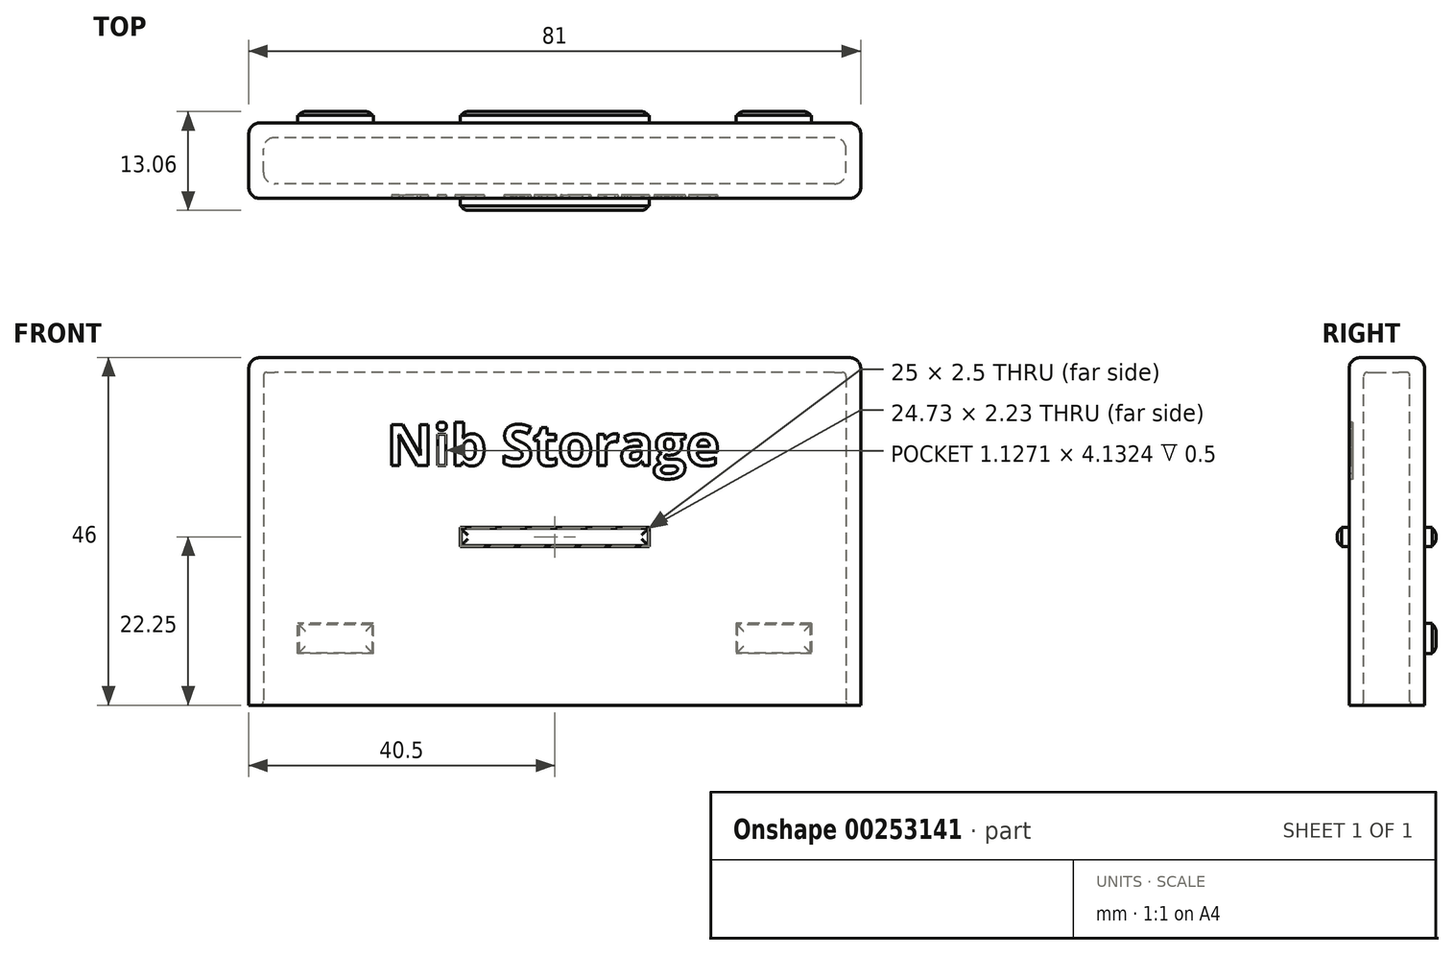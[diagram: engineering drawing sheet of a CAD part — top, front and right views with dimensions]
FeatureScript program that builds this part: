
annotation { "Feature Type Name" : "Feature", "Feature Type Description" : "" }
export const myFeature = defineFeature(function(context is Context, id is Id, definition is map)
    precondition{}
    {
        {
            var Q0;
            Q0=qCreatedBy(makeId("Top.planeOp"),FACE);
            var sketch = newSketch(context, id + "F0", { "sketchPlane" : qUnion([Q0])});
            skLineSegment(sketch, "E0.bottom", {"start": v(40.5, -5) * mm, "end": v(-40.5, -5) * mm});
            skLineSegment(sketch, "E0.top", {"start": v(40.5, 5) * mm, "end": v(-40.5, 5) * mm});
            skLineSegment(sketch, "E0.left", {"start": v(40.5, -5) * mm, "end": v(40.5, 5) * mm});
            skLineSegment(sketch, "E0.right", {"start": v(-40.5, -5) * mm, "end": v(-40.5, 5) * mm});
            skPoint(sketch, "E0.middle", {"position": v(0, 0) * mm});
            skSolve(sketch);
        }
        {
            var Q0;
            Q0=qSketchRegion(id+"F0",true);
            extrude(context, id + "F1", {"entities" : qUnion([Q0]), "depth" : 46 * mm});
        }
        {
            var Q0;
            Q0=makeQuery(id+"F1.opExtrude","CAP_EDGE",EDGE,{"disambiguationData":[OSD([sQuery(id+"F0.wireOp",EDGE,"E0.top")])],"isStart":false});
            var Q1;
            Q1=makeQuery(id+"F1.opExtrude","CAP_EDGE",EDGE,{"disambiguationData":[OSD([sQuery(id+"F0.wireOp",EDGE,"E0.bottom")])],"isStart":false});
            var Q2;
            Q2=makeQuery(id+"F1.opExtrude","CAP_EDGE",EDGE,{"disambiguationData":[OSD([sQuery(id+"F0.wireOp",EDGE,"E0.right")])],"isStart":false});
            var Q3;
            Q3=makeQuery(id+"F1.opExtrude","CAP_EDGE",EDGE,{"disambiguationData":[OSD([sQuery(id+"F0.wireOp",EDGE,"E0.left")])],"isStart":false});
            var Q4;
            Q4=makeQuery(id+"F1.opExtrude","SWEPT_EDGE",EDGE,{"disambiguationData":[OSD([sQuery(id+"F0.wireOp",EDGE,"E0.top"),sQuery(id+"F0.wireOp",EDGE,"E0.right")])]});
            var Q5;
            Q5=makeQuery(id+"F1.opExtrude","SWEPT_EDGE",EDGE,{"disambiguationData":[OSD([sQuery(id+"F0.wireOp",EDGE,"E0.bottom"),sQuery(id+"F0.wireOp",EDGE,"E0.right")])]});
            var Q6;
            Q6=makeQuery(id+"F1.opExtrude","SWEPT_EDGE",EDGE,{"disambiguationData":[OSD([sQuery(id+"F0.wireOp",EDGE,"E0.top"),sQuery(id+"F0.wireOp",EDGE,"E0.left")])]});
            var Q7;
            Q7=makeQuery(id+"F1.opExtrude","SWEPT_EDGE",EDGE,{"disambiguationData":[OSD([sQuery(id+"F0.wireOp",EDGE,"E0.bottom"),sQuery(id+"F0.wireOp",EDGE,"E0.left")])]});
            fillet(context, id + "F2", {"entities" : qUnion([Q0, Q1, Q2, Q3, Q4, Q5, Q6, Q7]), "radius" : 1.5 * mm, "tangentPropagation" : true, "allowEdgeOverflow" : false});
        }
        {
            var Q0;
            Q0=makeQuery(id+"F1.opExtrude","CAP_FACE",FACE,{"disambiguationData":[OSD([sQuery(id+"F0.wireOp",EDGE,"E0.bottom"),sQuery(id+"F0.wireOp",EDGE,"E0.top"),sQuery(id+"F0.wireOp",EDGE,"E0.left"),sQuery(id+"F0.wireOp",EDGE,"E0.right")])],"isStart":true});
            shell(context, id + "F3", {"entities" : qUnion([Q0]), "thickness" : 1.94 * mm});
        }
        {
            var Q0;
            Q0=makeQuery(id+"F3.opShell","OFFSET_EDGE",EDGE,{"disambiguationData":[OSD([sQuery(id+"F0.wireOp",EDGE,"E0.top"),sQuery(id+"F0.wireOp",EDGE,"E0.left")])]});
            var Q1;
            Q1=makeQuery(id+"F3.opShell","OFFSET_EDGE",EDGE,{"disambiguationData":[OSD([sQuery(id+"F0.wireOp",EDGE,"E0.bottom"),sQuery(id+"F0.wireOp",EDGE,"E0.left")])]});
            var Q2;
            Q2=makeQuery(id+"F3.opShell","OFFSET_EDGE",EDGE,{"disambiguationData":[OSD([sQuery(id+"F0.wireOp",EDGE,"E0.bottom"),sQuery(id+"F0.wireOp",EDGE,"E0.right")])]});
            var Q3;
            Q3=makeQuery(id+"F3.opShell","OFFSET_EDGE",EDGE,{"disambiguationData":[OSD([sQuery(id+"F0.wireOp",EDGE,"E0.top"),sQuery(id+"F0.wireOp",EDGE,"E0.right")])]});
            fillet(context, id + "F4", {"entities" : qUnion([Q0, Q1, Q2, Q3]), "radius" : 1.5 * mm, "tangentPropagation" : true, "allowEdgeOverflow" : false});
        }
        {
            var Q0;
            Q0=makeQuery(id+"F1.opExtrude","SWEPT_FACE",FACE,{"disambiguationData":[OSD([sQuery(id+"F0.wireOp",EDGE,"E0.bottom")])]});
            var sketch = newSketch(context, id + "F5", { "sketchPlane" : qUnion([Q0])});
            skLineSegment(sketch, "E1", {"start": v(39, 22.25) * mm, "end": v(-39, 22.25) * mm, "construction": true});
            skLineSegment(sketch, "E2", {"start": v(0, 44.5) * mm, "end": v(0, 0) * mm, "construction": true});
            skLineSegment(sketch, "E3.bottom", {"start": v(-12.5, 23.5) * mm, "end": v(12.5, 23.5) * mm});
            skLineSegment(sketch, "E3.top", {"start": v(-12.5, 21) * mm, "end": v(12.5, 21) * mm});
            skLineSegment(sketch, "E3.left", {"start": v(-12.5, 23.5) * mm, "end": v(-12.5, 21) * mm});
            skLineSegment(sketch, "E3.right", {"start": v(12.5, 23.5) * mm, "end": v(12.5, 21) * mm});
            skPoint(sketch, "E3.middle", {"position": v(0, 22.25) * mm});
            skLineSegment(sketch, "E4", {"start": v(-39, 8.04) * mm, "end": v(39, 8.04) * mm, "construction": true});
            skSolve(sketch);
        }
        {
            var Q0;
            Q0=qSketchRegion(id+"F5",true);
            extrude(context, id + "F6", {"entities" : qUnion([Q0]), "operationType" : NewBodyOperationType.ADD, "depth" : 1.56 * mm});
        }
        {
            var Q0;
            Q0=makeQuery(id+"F6.opExtrude","CAP_EDGE",EDGE,{"disambiguationData":[OSD([sQuery(id+"F5.wireOp",EDGE,"E3.bottom")])],"isStart":false});
            var Q1;
            Q1=makeQuery(id+"F6.opExtrude","CAP_EDGE",EDGE,{"disambiguationData":[OSD([sQuery(id+"F5.wireOp",EDGE,"E3.right")])],"isStart":false});
            var Q2;
            Q2=makeQuery(id+"F6.opExtrude","CAP_EDGE",EDGE,{"disambiguationData":[OSD([sQuery(id+"F5.wireOp",EDGE,"E3.top")])],"isStart":false});
            var Q3;
            Q3=makeQuery(id+"F6.opExtrude","CAP_EDGE",EDGE,{"disambiguationData":[OSD([sQuery(id+"F5.wireOp",EDGE,"E3.left")])],"isStart":false});
            var Q4;
            Q4=makeQuery(id+"F6.opExtrude","CAP_EDGE",EDGE,{"disambiguationData":[OSD([sQuery(id+"F5.wireOp",EDGE,"PPb5qhu8-9LVF-MKHu-zQhD-LhnvQhcufIGx.top")])],"isStart":false});
            var Q5;
            Q5=makeQuery(id+"F6.opExtrude","CAP_EDGE",EDGE,{"disambiguationData":[OSD([sQuery(id+"F5.wireOp",EDGE,"PPb5qhu8-9LVF-MKHu-zQhD-LhnvQhcufIGx.left")])],"isStart":false});
            var Q6;
            Q6=makeQuery(id+"F6.opExtrude","CAP_EDGE",EDGE,{"disambiguationData":[OSD([sQuery(id+"F5.wireOp",EDGE,"PPb5qhu8-9LVF-MKHu-zQhD-LhnvQhcufIGx.right")])],"isStart":false});
            var Q7;
            Q7=makeQuery(id+"F6.opExtrude","CAP_EDGE",EDGE,{"disambiguationData":[OSD([sQuery(id+"F5.wireOp",EDGE,"RZCc3H5M-QmGw-o7o6-KQUz-1ymlxaeq3NIj.left")])],"isStart":false});
            var Q8;
            Q8=makeQuery(id+"F6.opExtrude","CAP_EDGE",EDGE,{"disambiguationData":[OSD([sQuery(id+"F5.wireOp",EDGE,"RZCc3H5M-QmGw-o7o6-KQUz-1ymlxaeq3NIj.bottom")])],"isStart":false});
            var Q9;
            Q9=makeQuery(id+"F6.opExtrude","CAP_EDGE",EDGE,{"disambiguationData":[OSD([sQuery(id+"F5.wireOp",EDGE,"RZCc3H5M-QmGw-o7o6-KQUz-1ymlxaeq3NIj.right")])],"isStart":false});
            var Q10;
            Q10=makeQuery(id+"F6.opExtrude","CAP_EDGE",EDGE,{"disambiguationData":[OSD([sQuery(id+"F5.wireOp",EDGE,"RZCc3H5M-QmGw-o7o6-KQUz-1ymlxaeq3NIj.top")])],"isStart":false});
            var Q11;
            Q11=makeQuery(id+"F6.opExtrude","CAP_EDGE",EDGE,{"disambiguationData":[OSD([sQuery(id+"F5.wireOp",EDGE,"PPb5qhu8-9LVF-MKHu-zQhD-LhnvQhcufIGx.bottom")])],"isStart":false});
            fillet(context, id + "F7", {"entities" : qUnion([Q0, Q1, Q2, Q3, Q4, Q5, Q6, Q7, Q8, Q9, Q10, Q11]), "radius" : 1 * mm, "tangentPropagation" : true, "allowEdgeOverflow" : false});
        }
        {
            var Q0;
            Q0=makeQuery(id+"F1.opExtrude","SWEPT_FACE",FACE,{"disambiguationData":[OSD([sQuery(id+"F0.wireOp",EDGE,"E0.top")])]});
            var sketch = newSketch(context, id + "F8", { "sketchPlane" : qUnion([Q0])});
            skLineSegment(sketch, "E5", {"start": v(-39, 22.25) * mm, "end": v(-34.64, 22.25) * mm, "construction": true});
            skPoint(sketch, "E5.endSnap0", {"position": v(-39, 22.25) * mm});
            skLineSegment(sketch, "E6", {"start": v(39, 22.25) * mm, "end": v(-39, 22.25) * mm, "construction": true});
            skLineSegment(sketch, "E7", {"start": v(0, 44.5) * mm, "end": v(0, 0) * mm, "construction": true});
            skLineSegment(sketch, "E8.bottom", {"start": v(-12.5, 23.5) * mm, "end": v(12.5, 23.5) * mm});
            skLineSegment(sketch, "E8.top", {"start": v(-12.5, 21) * mm, "end": v(12.5, 21) * mm});
            skLineSegment(sketch, "E8.left", {"start": v(-12.5, 23.5) * mm, "end": v(-12.5, 21) * mm});
            skLineSegment(sketch, "E8.right", {"start": v(12.5, 23.5) * mm, "end": v(12.5, 21) * mm});
            skPoint(sketch, "E8.middle", {"position": v(0, 22.25) * mm});
            skLineSegment(sketch, "E9", {"start": v(39, 8.8) * mm, "end": v(-39, 8.8) * mm, "construction": true});
            skLineSegment(sketch, "E10.bottom", {"start": v(24, 6.8) * mm, "end": v(34, 6.8) * mm});
            skLineSegment(sketch, "E10.top", {"start": v(24, 10.8) * mm, "end": v(34, 10.8) * mm});
            skLineSegment(sketch, "E10.left", {"start": v(24, 6.8) * mm, "end": v(24, 10.8) * mm});
            skLineSegment(sketch, "E10.right", {"start": v(34, 6.8) * mm, "end": v(34, 10.8) * mm});
            skPoint(sketch, "E10.middle", {"position": v(29, 8.8) * mm});
            skLineSegment(sketch, "E11.bottom", {"start": v(-34, 10.8) * mm, "end": v(-24, 10.8) * mm});
            skLineSegment(sketch, "E11.top", {"start": v(-34, 6.8) * mm, "end": v(-24, 6.8) * mm});
            skLineSegment(sketch, "E11.left", {"start": v(-34, 10.8) * mm, "end": v(-34, 6.8) * mm});
            skLineSegment(sketch, "E11.right", {"start": v(-24, 10.8) * mm, "end": v(-24, 6.8) * mm});
            skPoint(sketch, "E11.middle", {"position": v(-29, 8.8) * mm});
            skSolve(sketch);
        }
        {
            var Q0;
            Q0=qSketchRegion(id+"F8",true);
            extrude(context, id + "F9", {"entities" : qUnion([Q0]), "operationType" : NewBodyOperationType.ADD, "depth" : 1.5 * mm});
        }
        {
            var Q0;
            Q0=makeQuery(id+"F9.opExtrude","CAP_EDGE",EDGE,{"disambiguationData":[OSD([sQuery(id+"F8.wireOp",EDGE,"E8.bottom")])],"isStart":false});
            var Q1;
            Q1=makeQuery(id+"F9.opExtrude","CAP_EDGE",EDGE,{"disambiguationData":[OSD([sQuery(id+"F8.wireOp",EDGE,"E8.top")])],"isStart":false});
            var Q2;
            Q2=makeQuery(id+"F9.opExtrude","CAP_EDGE",EDGE,{"disambiguationData":[OSD([sQuery(id+"F8.wireOp",EDGE,"E8.left")])],"isStart":false});
            var Q3;
            Q3=makeQuery(id+"F9.opExtrude","CAP_EDGE",EDGE,{"disambiguationData":[OSD([sQuery(id+"F8.wireOp",EDGE,"E8.right")])],"isStart":false});
            var Q4;
            Q4=makeQuery(id+"F9.opExtrude","CAP_EDGE",EDGE,{"disambiguationData":[OSD([sQuery(id+"F8.wireOp",EDGE,"E11.top")])],"isStart":false});
            var Q5;
            Q5=makeQuery(id+"F9.opExtrude","CAP_EDGE",EDGE,{"disambiguationData":[OSD([sQuery(id+"F8.wireOp",EDGE,"E11.bottom")])],"isStart":false});
            var Q6;
            Q6=makeQuery(id+"F9.opExtrude","CAP_EDGE",EDGE,{"disambiguationData":[OSD([sQuery(id+"F8.wireOp",EDGE,"E11.right")])],"isStart":false});
            var Q7;
            Q7=makeQuery(id+"F9.opExtrude","CAP_FACE",FACE,{"disambiguationData":[OSD([sQuery(id+"F8.wireOp",EDGE,"E11.bottom"),sQuery(id+"F8.wireOp",EDGE,"E11.top"),sQuery(id+"F8.wireOp",EDGE,"E11.left"),sQuery(id+"F8.wireOp",EDGE,"E11.right")])],"isStart":false});
            var Q8;
            Q8=makeQuery(id+"F9.opExtrude","CAP_EDGE",EDGE,{"disambiguationData":[OSD([sQuery(id+"F8.wireOp",EDGE,"E10.left")])],"isStart":false});
            var Q9;
            Q9=makeQuery(id+"F9.opExtrude","CAP_EDGE",EDGE,{"disambiguationData":[OSD([sQuery(id+"F8.wireOp",EDGE,"E10.right")])],"isStart":false});
            var Q10;
            Q10=makeQuery(id+"F9.opExtrude","CAP_EDGE",EDGE,{"disambiguationData":[OSD([sQuery(id+"F8.wireOp",EDGE,"E10.top")])],"isStart":false});
            var Q11;
            Q11=makeQuery(id+"F9.opExtrude","CAP_EDGE",EDGE,{"disambiguationData":[OSD([sQuery(id+"F8.wireOp",EDGE,"E10.bottom")])],"isStart":false});
            fillet(context, id + "F10", {"entities" : qUnion([Q0, Q1, Q2, Q3, Q4, Q5, Q6, Q7, Q8, Q9, Q10, Q11]), "radius" : 1 * mm, "tangentPropagation" : true, "allowEdgeOverflow" : false});
        }
        {
            var Q0;
            Q0=makeQuery(id+"F3.opShell","OFFSET_FACE",FACE,{"disambiguationData":[OSD([sQuery(id+"F0.wireOp",EDGE,"E0.left")])]});
            fillet(context, id + "F11", {"entities" : qUnion([Q0]), "radius" : .5 * mm, "tangentPropagation" : true, "allowEdgeOverflow" : false});
        }
        {
            var Q0;
            Q0=qSketchRegion(id+"F8",true);
            extrude(context, id + "F12", {"entities" : qUnion([Q0]), "operationType" : NewBodyOperationType.ADD, "depth" : 1 * mm});
        }
        {
            var Q0;
            Q0=qSketchRegion(id+"F5",true);
            extrude(context, id + "F13", {"entities" : qUnion([Q0]), "operationType" : NewBodyOperationType.ADD, "depth" : 1 * mm});
        }
        {
            var Q0;
            Q0=makeQuery(id+"F5.imprint","IMPRINT",FACE,{"disambiguationData":[TD([[makeQuery(id+"F5.imprint","IMPRINT",EDGE,{"derivedFrom":sQuery(id+"F5.wireOp",EDGE,"E3.bottom")}),1.0]])]});
            var sketch = newSketch(context, id + "F14", { "sketchPlane" : qUnion([Q0])});
            skText(sketch, "E12", { "text": "Nib Storage\n", "fontName": "OpenSans-Bold.ttf"});
            const initialGuessF14  = {"E12": [-0.02226, 0.03171, 1, 0, 0.00545]};
            skSetInitialGuess(sketch, initialGuessF14);
            skSolve(sketch);
        }
        {
            var Q0;
            Q0=qSketchRegion(id+"F14",true);
            extrude(context, id + "F15", {"entities" : qUnion([Q0]), "operationType" : NewBodyOperationType.REMOVE, "oppositeDirection" : true, "depth" : .5 * mm});
        }
    });
